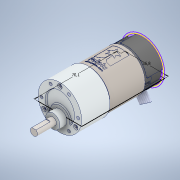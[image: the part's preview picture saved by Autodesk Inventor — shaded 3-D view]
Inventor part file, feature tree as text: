
AUTODESK INVENTOR PART (.ipt)
format: ipt  version: 2020 (Build 240168000, 168)  size: 1,469,440 bytes
history: native  units: in
note: dims shown in document units (in); Inventor stores cm internally (conversion verified against a paired STEP export)
features: sketch x2, other x1
ambient origin geometry x8: Origin, YZ Plane, XZ Plane, XY Plane, X Axis, Y Axis, Z Axis, Center Point
bodies: Solid1 (feature_tree)
feature tree (3):
  sketch  "Sketch1"  dims[d0=1.4488in]
  sketch  "Sketch2"  dims[d1=2.7598in]
  other  "Combine-with encoder and case"
